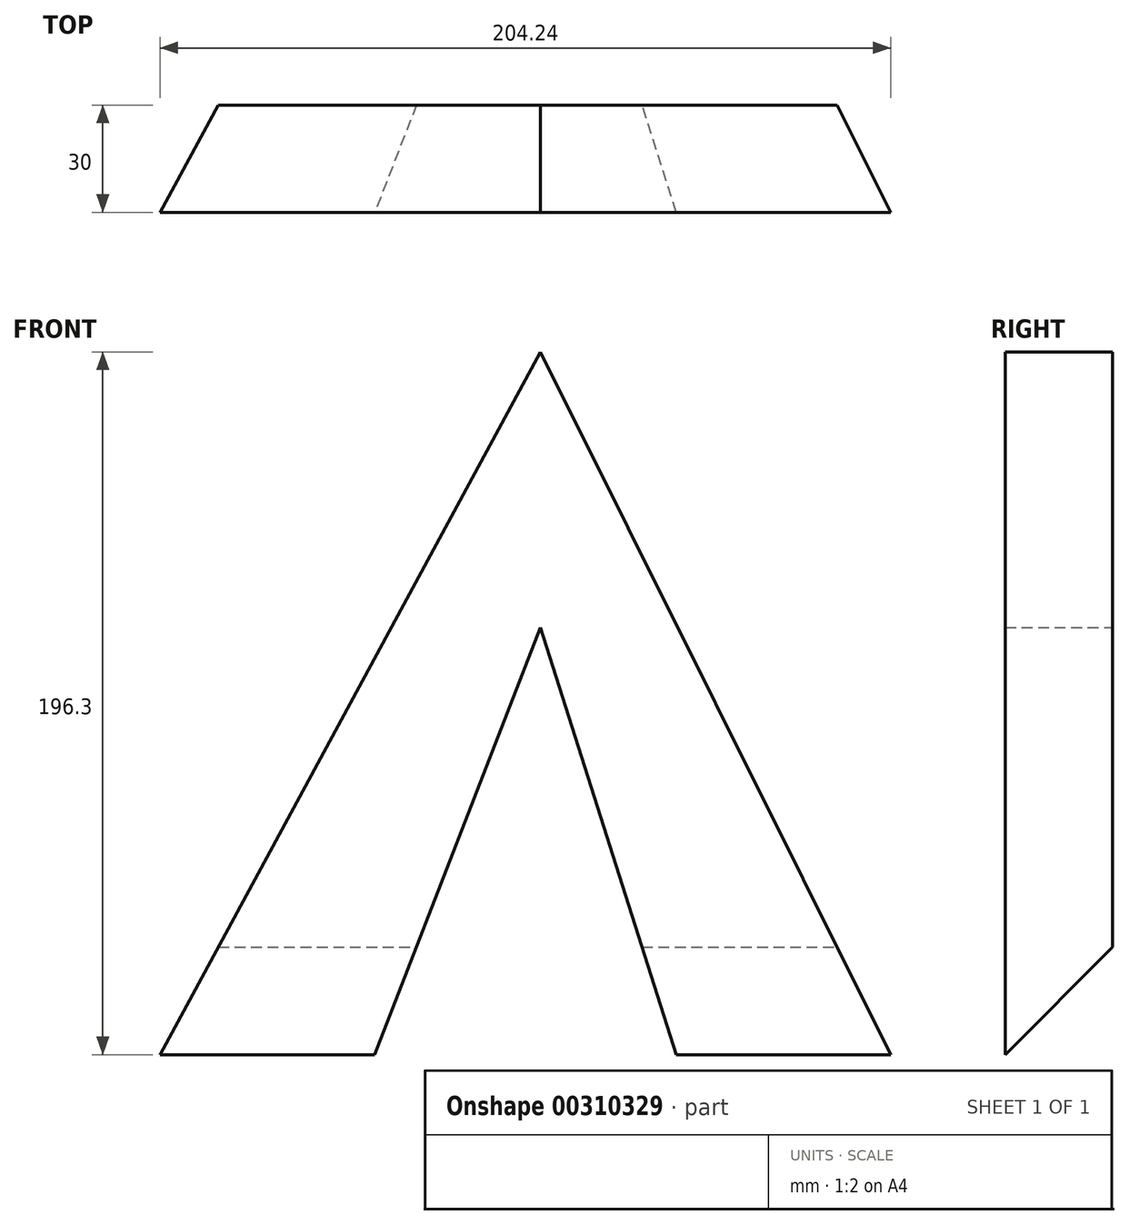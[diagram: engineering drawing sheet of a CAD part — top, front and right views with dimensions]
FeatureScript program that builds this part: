
annotation { "Feature Type Name" : "Feature", "Feature Type Description" : "" }
export const myFeature = defineFeature(function(context is Context, id is Id, definition is map)
    precondition{}
    {
        {
            var Q0;
            Q0=qCreatedBy(makeId("Front.planeOp"),FACE);
            var sketch = newSketch(context, id + "F0", { "sketchPlane" : qUnion([Q0])});
            skLineSegment(sketch, "E0.bottom", {"start": v(-106.3, -119.28) * mm, "end": v(-46.3, -119.28) * mm});
            skLineSegment(sketch, "E1", {"start": v(-106.3, -119.28) * mm, "end": v(0, 77.02) * mm});
            skLineSegment(sketch, "E2", {"start": v(0, 77.02) * mm, "end": v(97.95, -119.28) * mm});
            skPoint(sketch, "E0.left.end.orphan", {"position": v(-106.3, 75.7) * mm});
            skPoint(sketch, "E0.right.end.orphan", {"position": v(106.3, 78.34) * mm});
            skLineSegment(sketch, "E3", {"start": v(-46.3, -119.28) * mm, "end": v(0, 0) * mm});
            skLineSegment(sketch, "E4", {"start": v(0, 0) * mm, "end": v(37.95, -119.28) * mm});
            skLineSegment(sketch, "E5.trimOffspring", {"start": v(37.95, -119.28) * mm, "end": v(97.95, -119.28) * mm});
            skSolve(sketch);
        }
        {
            var Q0;
            Q0 = qSketchRegion(id + "F0", true);
            extrude(context, id + "F1", {"entities" : qUnion([Q0]), "depth" : 30 * mm});
        }
        {
            var Q0;
            Q0=qCreatedBy(makeId("Right.planeOp"),FACE);
            var sketch = newSketch(context, id + "F2", { "sketchPlane" : qUnion([Q0])});
            skPoint(sketch, "E6", {"position": v(-30, -119.28) * mm});
            skLineSegment(sketch, "E7", {"start": v(-30, -119.28) * mm, "end": v(0.56, -88.72) * mm});
            skLineSegment(sketch, "E8", {"start": v(0.56, -88.72) * mm, "end": v(0.56, -121.19) * mm});
            skLineSegment(sketch, "E9", {"start": v(0.56, -121.19) * mm, "end": v(-30, -121.19) * mm});
            skLineSegment(sketch, "E10", {"start": v(-30, -121.19) * mm, "end": v(-30, -119.28) * mm});
            skSolve(sketch);
        }
        {
            var Q0;
            Q0=makeQuery(id+"F2.imprint","IMPRINT",FACE,{"disambiguationData":[TD([[makeQuery(id+"F2.imprint","IMPRINT",EDGE,{"derivedFrom":sQuery(id+"F2.wireOp",EDGE,"E7")}),-1.0]])]});
            extrude(context, id + "F3", {"entities" : qUnion([Q0]), "operationType" : NewBodyOperationType.REMOVE, "endBound" : BoundingType.SYMMETRIC, "oppositeDirection" : true, "depth" : 348 * mm});
        }
    });
